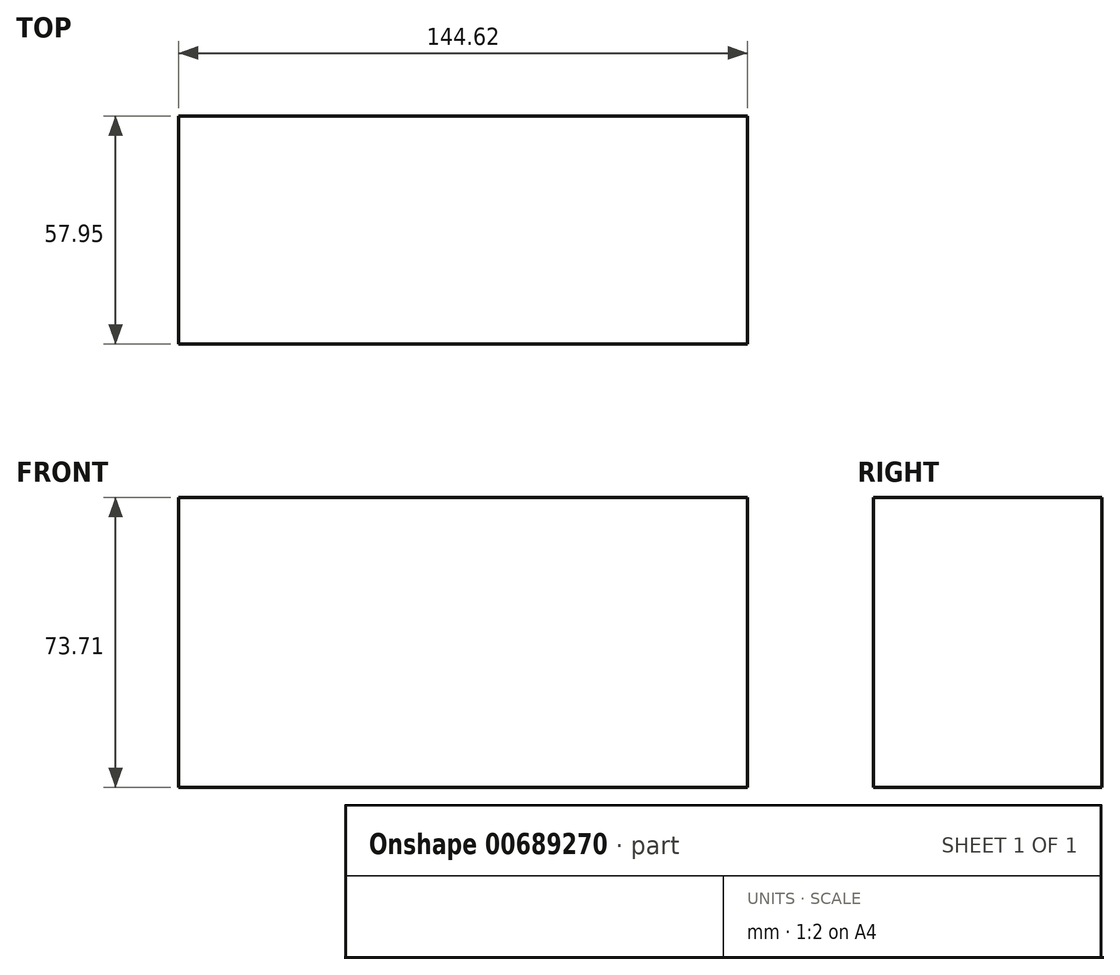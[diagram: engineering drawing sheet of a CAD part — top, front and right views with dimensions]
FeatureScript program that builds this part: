
annotation { "Feature Type Name" : "Feature", "Feature Type Description" : "" }
export const myFeature = defineFeature(function(context is Context, id is Id, definition is map)
    precondition{}
    {
        {
            var Q0;
            Q0=qCreatedBy(makeId("Front.planeOp"),FACE);
            var sketch = newSketch(context, id + "F0", { "sketchPlane" : qUnion([Q0])});
            skLineSegment(sketch, "E0.bottom", {"start": v(29.94, 0) * mm, "end": v(-114.68, 0) * mm});
            skLineSegment(sketch, "E0.top", {"start": v(29.94, -73.71) * mm, "end": v(-114.68, -73.71) * mm});
            skLineSegment(sketch, "E0.left", {"start": v(29.94, 0) * mm, "end": v(29.94, -73.71) * mm});
            skLineSegment(sketch, "E0.right", {"start": v(-114.68, 0) * mm, "end": v(-114.68, -73.71) * mm});
            skLineSegment(sketch, "E1.bottom", {"start": v(-70.35, -86.87) * mm, "end": v(-114.43, -86.87) * mm});
            skLineSegment(sketch, "E1.top", {"start": v(-70.35, -124.22) * mm, "end": v(-114.43, -124.22) * mm});
            skLineSegment(sketch, "E1.left", {"start": v(-70.35, -86.87) * mm, "end": v(-70.35, -124.22) * mm});
            skLineSegment(sketch, "E1.right", {"start": v(-114.43, -86.87) * mm, "end": v(-114.43, -124.22) * mm});
            skLineSegment(sketch, "E2.bottom", {"start": v(-13.73, 30.15) * mm, "end": v(105.27, 30.15) * mm});
            skLineSegment(sketch, "E2.top", {"start": v(-13.73, 110.75) * mm, "end": v(105.27, 110.75) * mm});
            skLineSegment(sketch, "E2.left", {"start": v(-13.73, 30.15) * mm, "end": v(-13.73, 110.75) * mm});
            skLineSegment(sketch, "E2.right", {"start": v(105.27, 30.15) * mm, "end": v(105.27, 110.75) * mm});
            skLineSegment(sketch, "E3.bottom", {"start": v(93.65, 0) * mm, "end": v(0, 0) * mm});
            skLineSegment(sketch, "E3.top", {"start": v(93.65, 0) * mm, "end": v(0, 0) * mm});
            skLineSegment(sketch, "E3.left", {"start": v(93.65, 0) * mm, "end": v(93.65, 0) * mm});
            skLineSegment(sketch, "E3.right", {"start": v(0, 0) * mm, "end": v(0, 0) * mm});
            skSolve(sketch);
        }
        {
            var Q0;
            {var subQ2=sQuery(id+"F0.wireOp",EDGE,"E0.bottom");Q0=makeQuery(id+"F0.imprint","IMPRINT",FACE,{"disambiguationData":[TD([[makeQuery(id+"F0.imprint","IMPRINT",EDGE,{"derivedFrom":subQ2}),1.0]])]});}
            extrude(context, id + "F1", {"entities" : qUnion([Q0]), "oppositeDirection" : true, "depth" : 57.95 * mm, "offsetDistance" : 25.4 * mm});
        }
    });
